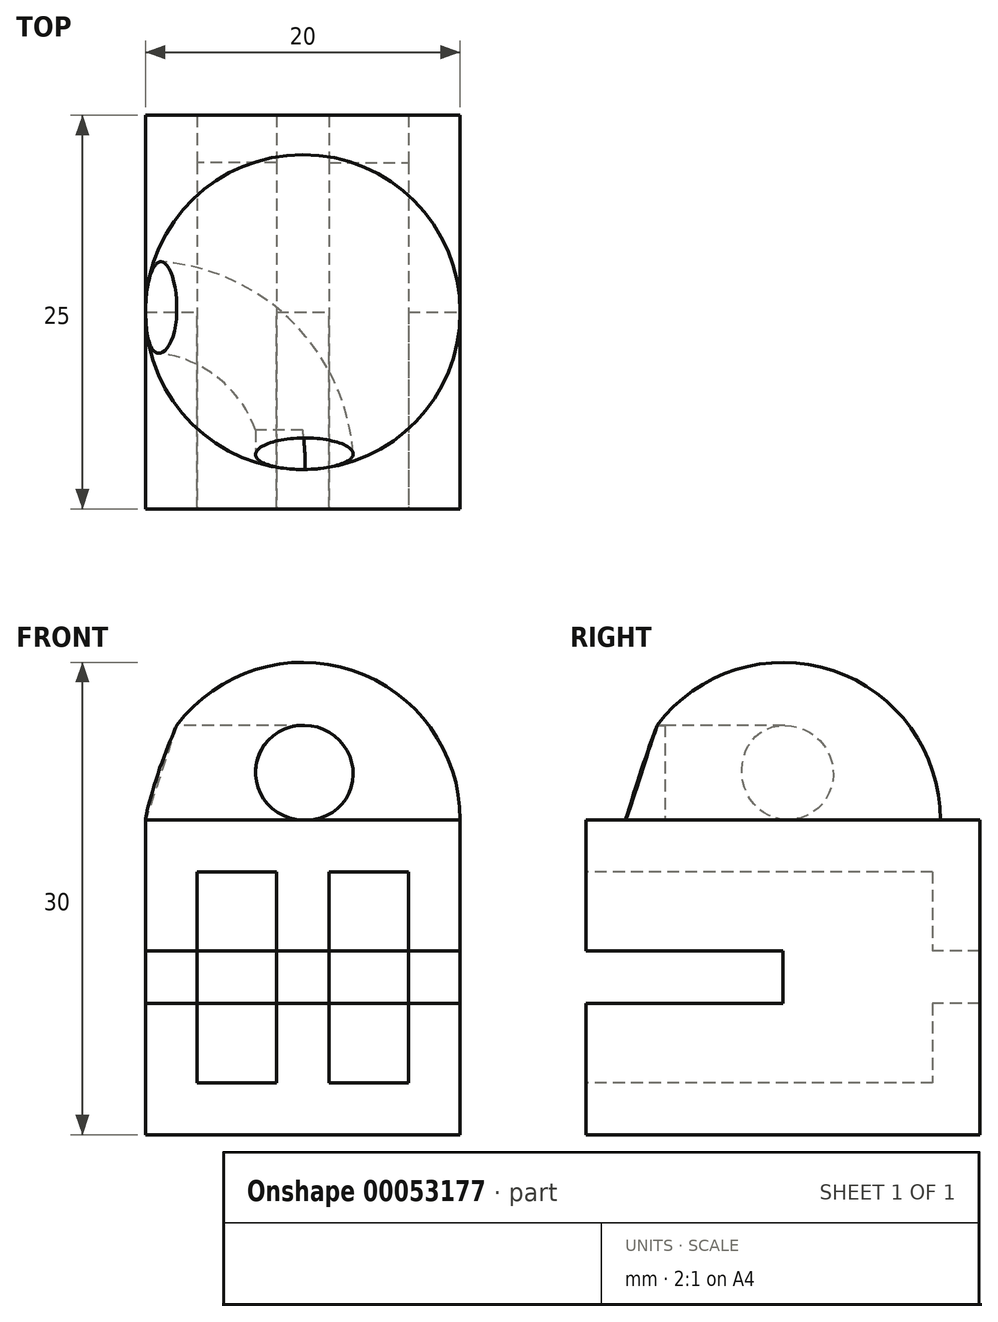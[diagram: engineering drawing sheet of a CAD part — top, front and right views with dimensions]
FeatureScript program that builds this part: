
annotation { "Feature Type Name" : "Feature", "Feature Type Description" : "" }
export const myFeature = defineFeature(function(context is Context, id is Id, definition is map)
    precondition{}
    {
        {
            var Q0;
            Q0=qCreatedBy(makeId("Front.planeOp"),FACE);
            var sketch = newSketch(context, id + "F0", { "sketchPlane" : qUnion([Q0])});
            skLineSegment(sketch, "E0.bottom", {"start": v(0, 0) * mm, "end": v(20, 0) * mm});
            skLineSegment(sketch, "E0.top", {"start": v(0, 20) * mm, "end": v(20, 20) * mm});
            skLineSegment(sketch, "E0.left", {"start": v(0, 0) * mm, "end": v(0, 20) * mm});
            skLineSegment(sketch, "E0.right", {"start": v(20, 0) * mm, "end": v(20, 20) * mm});
            skSolve(sketch);
        }
        {
            var Q0;
            Q0=makeQuery(id+"F0.imprint","IMPRINT",FACE,{"disambiguationData":[TD([[makeQuery(id+"F0.imprint","IMPRINT",EDGE,{"derivedFrom":sQuery(id+"F0.wireOp",EDGE,"E0.bottom")}),1.0]])]});
            extrude(context, id + "F1", {"entities" : qUnion([Q0]), "depth" : 25 * mm});
        }
        {
            var Q0;
            Q0=makeQuery(id+"F1.opExtrude","CAP_FACE",FACE,{"disambiguationData":[OSD([sQuery(id+"F0.wireOp",EDGE,"E0.bottom"),sQuery(id+"F0.wireOp",EDGE,"E0.top"),sQuery(id+"F0.wireOp",EDGE,"E0.left"),sQuery(id+"F0.wireOp",EDGE,"E0.right")])],"isStart":false});
            var sketch = newSketch(context, id + "F2", { "sketchPlane" : qUnion([Q0])});
            skLineSegment(sketch, "E1.rect.bottom", {"start": v(3.3, 16.7) * mm, "end": v(16.7, 16.7) * mm});
            skLineSegment(sketch, "E1.rect.top", {"start": v(3.3, 3.3) * mm, "end": v(16.7, 3.3) * mm});
            skLineSegment(sketch, "E1.rect.left", {"start": v(3.3, 16.7) * mm, "end": v(3.3, 3.3) * mm});
            skLineSegment(sketch, "E1.rect.right", {"start": v(16.7, 16.7) * mm, "end": v(16.7, 3.3) * mm});
            skPoint(sketch, "E1.rect.middle", {"position": v(10, 10) * mm});
            skPoint(sketch, "E1.rect.middle.positionSnap0", {"position": v(10, 20) * mm});
            skPoint(sketch, "E1.rect.middle.positionSnap1", {"position": v(0, 10) * mm});
            skPoint(sketch, "E1.rect.centerSnap0", {"position": v(10, 20) * mm});
            skPoint(sketch, "E1.rect.centerSnap1", {"position": v(0, 10) * mm});
            skSolve(sketch);
        }
        {
            var Q0;
            Q0=makeQuery(id+"F2.imprint","IMPRINT",FACE,{"disambiguationData":[TD([[makeQuery(id+"F2.imprint","IMPRINT",EDGE,{"derivedFrom":sQuery(id+"F2.wireOp",EDGE,"E1.rect.bottom")}),-1.0]])]});
            extrude(context, id + "F3", {"entities" : qUnion([Q0]), "operationType" : NewBodyOperationType.REMOVE, "oppositeDirection" : true, "depth" : 22 * mm});
        }
        {
            var Q0;
            Q0=makeQuery(id+"F1.opExtrude","CAP_FACE",FACE,{"disambiguationData":[OSD([sQuery(id+"F0.wireOp",EDGE,"E0.bottom"),sQuery(id+"F0.wireOp",EDGE,"E0.top"),sQuery(id+"F0.wireOp",EDGE,"E0.left"),sQuery(id+"F0.wireOp",EDGE,"E0.right")])],"isStart":false});
            var sketch = newSketch(context, id + "F4", { "sketchPlane" : qUnion([Q0])});
            skLineSegment(sketch, "E2", {"start": v(11.67, 16.7) * mm, "end": v(11.67, 3.3) * mm});
            skLineSegment(sketch, "E3", {"start": v(8.33, 3.3) * mm, "end": v(8.33, 16.7) * mm});
            skSolve(sketch);
        }
        {
            var Q0;
            {var subQ0=sQuery(id+"F4.wireOp",EDGE,"E2");Q0=makeQuery(id+"F4.imprint","IMPRINT",FACE,{"disambiguationData":[TD([[makeQuery(id+"F4.imprint","IMPRINT",EDGE,{"derivedFrom":subQ0}),-1.0]])]});}
            extrude(context, id + "F5", {"entities" : qUnion([Q0]), "operationType" : NewBodyOperationType.ADD, "oppositeDirection" : true, "depth" : 25 * mm});
        }
        {
            var Q0;
            Q0=makeQuery(id+"F1.opExtrude","SWEPT_FACE",FACE,{"disambiguationData":[OSD([sQuery(id+"F0.wireOp",EDGE,"E0.right")])]});
            var sketch = newSketch(context, id + "F6", { "sketchPlane" : qUnion([Q0])});
            skLineSegment(sketch, "E4", {"start": v(-25, 10) * mm, "end": v(-12.5, 10) * mm});
            skLineSegment(sketch, "E5", {"start": v(-12.5, 11.67) * mm, "end": v(-25, 11.67) * mm});
            skLineSegment(sketch, "E6", {"start": v(-25, 8.33) * mm, "end": v(-12.5, 8.33) * mm});
            skLineSegment(sketch, "E7", {"start": v(-12.5, 11.67) * mm, "end": v(-12.5, 8.33) * mm});
            skSolve(sketch);
        }
        {
            var Q0;
            {var subQ0=sQuery(id+"F6.wireOp",EDGE,"E4");Q0=makeQuery(id+"F6.imprint","IMPRINT",FACE,{"disambiguationData":[TD([[makeQuery(id+"F6.imprint","IMPRINT",EDGE,{"derivedFrom":subQ0}),1.0]])]});}
            var Q1;
            {var subQ0=sQuery(id+"F6.wireOp",EDGE,"E4");Q1=makeQuery(id+"F6.imprint","IMPRINT",FACE,{"disambiguationData":[TD([[makeQuery(id+"F6.imprint","IMPRINT",EDGE,{"derivedFrom":subQ0}),-1.0]])]});}
            extrude(context, id + "F7", {"entities" : qUnion([Q0, Q1]), "operationType" : NewBodyOperationType.REMOVE, "oppositeDirection" : true, "depth" : 25 * mm});
        }
        {
            var Q0;
            Q0=makeQuery(id+"F1.opExtrude","SWEPT_FACE",FACE,{"disambiguationData":[OSD([sQuery(id+"F0.wireOp",EDGE,"E0.top")])]});
            var sketch = newSketch(context, id + "F8", { "sketchPlane" : qUnion([Q0])});
            skLineSegment(sketch, "E8", {"start": v(0, -12.5) * mm, "end": v(10, -12.5) * mm});
            skPoint(sketch, "E8.endSnap0", {"position": v(10, 0) * mm});
            skCircle(sketch, "E9", {"center": v(10, -12.5) * mm, "radius": 10 * mm});
            skLineSegment(sketch, "E10", {"start": v(10, -12.5) * mm, "end": v(10, -2.5) * mm});
            skLineSegment(sketch, "E11", {"start": v(10, -12.5) * mm, "end": v(10, -22.5) * mm});
            skLineSegment(sketch, "E12", {"start": v(10, -22.5) * mm, "end": v(20, -22.5) * mm});
            skSolve(sketch);
        }
        {
            var Q0;
            {var subQ0=sQuery(id+"F8.wireOp",EDGE,"E10");Q0=makeQuery(id+"F8.imprint","IMPRINT",FACE,{"disambiguationData":[TD([[makeQuery(id+"F8.imprint","IMPRINT",EDGE,{"derivedFrom":subQ0}),-1.0]])]});}
            var Q1;
            Q1=sQuery(id+"F8.wireOp",EDGE,"E10");
            revolve(context, id + "F9", {"operationType" : NewBodyOperationType.ADD, "entities" : qUnion([Q0]), "axis" : qUnion([Q1]), "revolveType" : RevolveType.ONE_DIRECTION, "oppositeDirection" : true, "angle" : 180 * degree});
        }
        {
            var Q0;
            Q0=makeQuery(id+"F1.opExtrude","SWEPT_FACE",FACE,{"disambiguationData":[OSD([sQuery(id+"F0.wireOp",EDGE,"E0.right")])]});
            var sketch = newSketch(context, id + "F10", { "sketchPlane" : qUnion([Q0])});
            skLineSegment(sketch, "E13", {"start": v(-22.5, 20) * mm, "end": v(-22.5, 23) * mm});
            skSolve(sketch);
        }
        {
            var Q0;
            Q0=sQuery(id+"F8.wireOp",EDGE,"E12");
            var Q1;
            Q1=sQuery(id+"F10.wireOp",EDGE,"E13");
            cPlane(context, id + "F11", {"entities" : qUnion([Q0, Q1]), "cplaneType" : CPlaneType.LINE_ANGLE, "offset" : 150 * mm, "angle" : 0 * degree, "width" : 150 * mm, "height" : 150 * mm});
        }
        {
            var Q0;
            {var subQ0=sQuery(id+"F2.wireOp",EDGE,"E1.rect.bottom");var subQ1=sQuery(id+"F0.wireOp",EDGE,"E0.right");var subQ2=sQuery(id+"F0.wireOp",EDGE,"E0.left");var subQ3=sQuery(id+"F0.wireOp",EDGE,"E0.top");var subQ4=sQuery(id+"F4.wireOp",EDGE,"E2");var subQ5=sQuery(id+"F4.wireOp",EDGE,"E3");Q0=makeQuery(id+"F7.boolean.opBoolean","SPLIT",FACE,{"disambiguationData":[TD([makeQuery(id+"F1.opExtrude","SWEPT_FACE",FACE,{"disambiguationData":[OSD([subQ3])]})])],"derivedFrom":makeQuery(id+"F5.boolean.opBoolean","MERGE",FACE,{"derivedFrom":[makeQuery(id+"F1.opExtrude","CAP_FACE",FACE,{"disambiguationData":[OSD([sQuery(id+"F0.wireOp",EDGE,"E0.bottom"),subQ3,subQ2,subQ1])],"isStart":false}),makeQuery(id+"F5.opExtrude","CAP_FACE",FACE,{"disambiguationData":[OSD([subQ0,sQuery(id+"F2.wireOp",EDGE,"E1.rect.top"),subQ4,subQ5])],"isStart":true})]})});}
            var sketch = newSketch(context, id + "F12", { "sketchPlane" : qUnion([Q0])});
            skLineSegment(sketch, "E14", {"start": v(10, 20) * mm, "end": v(10, 26) * mm});
            skCircle(sketch, "E15", {"center": v(10, 23) * mm, "radius": 3 * mm});
            skSolve(sketch);
        }
        {
            var Q0;
            {var subQ0=sQuery(id+"F12.wireOp",EDGE,"E14");Q0=makeQuery(id+"F12.imprint","IMPRINT",FACE,{"disambiguationData":[TD([[makeQuery(id+"F12.imprint","IMPRINT",EDGE,{"derivedFrom":subQ0}),1.0]])]});}
            var Q1;
            {var subQ0=sQuery(id+"F12.wireOp",EDGE,"E14");Q1=makeQuery(id+"F12.imprint","IMPRINT",FACE,{"disambiguationData":[TD([[makeQuery(id+"F12.imprint","IMPRINT",EDGE,{"derivedFrom":subQ0}),-1.0]])]});}
            extrude(context, id + "F13", {"entities" : qUnion([Q0, Q1]), "oppositeDirection" : true, "depth" : 5 * mm});
        }
        {
            var Q0;
            Q0=qCreatedBy(id+"F11.planeOp",FACE);
            var sketch = newSketch(context, id + "F14", { "sketchPlane" : qUnion([Q0])});
            skLineSegment(sketch, "E16", {"start": v(0, 0) * mm, "end": v(0, 20) * mm});
            skLineSegment(sketch, "E17", {"start": v(0, 20) * mm, "end": v(0, 20) * mm});
            skLineSegment(sketch, "E18", {"start": v(0, 20) * mm, "end": v(0, 23) * mm});
            skSolve(sketch);
        }
        {
            var Q0;
            Q0=makeQuery(id+"F13.opExtrude","CAP_FACE",FACE,{"disambiguationData":[OSD([sQuery(id+"F12.wireOp",EDGE,"E15")])],"isStart":false});
            var Q1;
            Q1=sQuery(id+"F14.wireOp",EDGE,"E18");
            revolve(context, id + "F15", {"operationType" : NewBodyOperationType.REMOVE, "entities" : qUnion([Q0]), "axis" : qUnion([Q1]), "revolveType" : RevolveType.FULL, "oppositeDirection" : true});
        }
        {
            var Q0;
            Q0=qSketchRegion(id+"F12",true);
            extrude(context, id + "F16", {"entities" : qUnion([Q0]), "operationType" : NewBodyOperationType.REMOVE, "oppositeDirection" : true, "depth" : 5 * mm});
        }
        {
            var Q0;
            Q0=makeQuery(id+"F7.boolean.opBoolean","COPY",FACE,{"disambiguationData":[TD([makeQuery(id+"F5.opExtrude","SWEPT_FACE",FACE,{"disambiguationData":[OSD([sQuery(id+"F4.wireOp",EDGE,"E2")])]})])],"derivedFrom":makeQuery(id+"F7.opExtrude","SWEPT_FACE",FACE,{"disambiguationData":[OSD([sQuery(id+"F6.wireOp",EDGE,"E7")])]})});
            var sketch = newSketch(context, id + "F17", { "sketchPlane" : qUnion([Q0])});
            skLineSegment(sketch, "E19", {"start": v(11.67, 11.67) * mm, "end": v(16.7, 11.67) * mm});
            skLineSegment(sketch, "E20", {"start": v(16.7, 11.67) * mm, "end": v(16.7, 8.33) * mm});
            skLineSegment(sketch, "E21", {"start": v(16.7, 8.33) * mm, "end": v(11.67, 8.33) * mm});
            skLineSegment(sketch, "E22", {"start": v(8.33, 8.33) * mm, "end": v(3.3, 8.33) * mm});
            skLineSegment(sketch, "E23", {"start": v(3.3, 8.33) * mm, "end": v(3.3, 11.67) * mm});
            skLineSegment(sketch, "E24", {"start": v(3.3, 11.67) * mm, "end": v(8.33, 11.67) * mm});
            skSolve(sketch);
        }
        {
            var Q0;
            Q0=makeQuery(id+"F17.imprint","IMPRINT",FACE,{"disambiguationData":[TD([[makeQuery(id+"F17.imprint","IMPRINT",EDGE,{"derivedFrom":sQuery(id+"F17.wireOp",EDGE,"E22")}),-1.0]])]});
            var Q1;
            Q1=makeQuery(id+"F17.imprint","IMPRINT",FACE,{"disambiguationData":[TD([[makeQuery(id+"F17.imprint","IMPRINT",EDGE,{"derivedFrom":sQuery(id+"F17.wireOp",EDGE,"E19")}),-1.0]])]});
            extrude(context, id + "F18", {"entities" : qUnion([Q0, Q1]), "operationType" : NewBodyOperationType.REMOVE, "oppositeDirection" : true, "depth" : 25 * mm});
        }
    });
